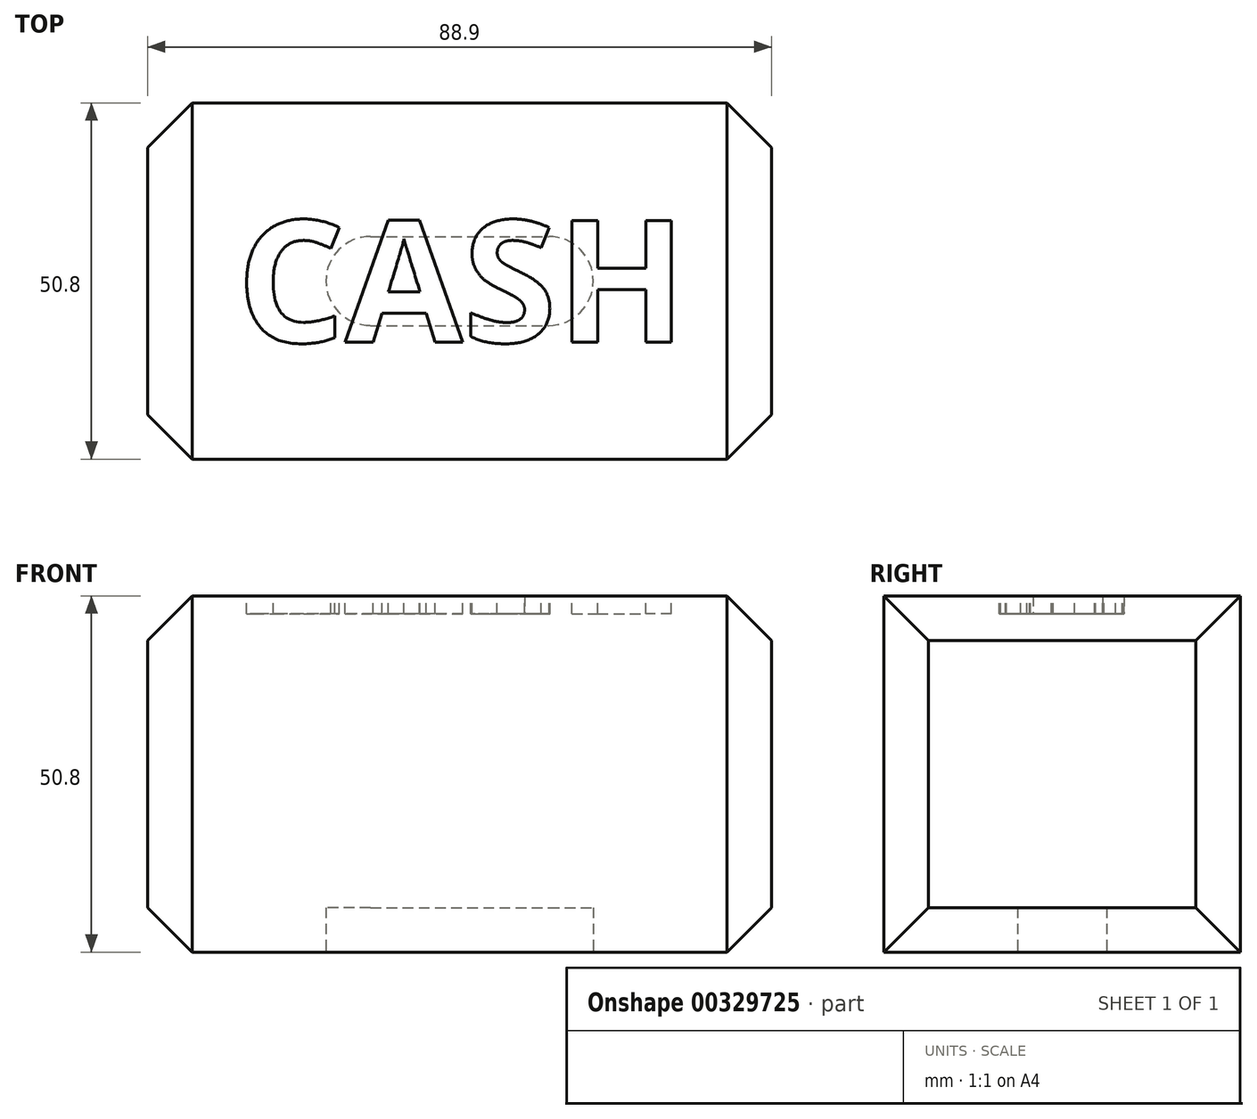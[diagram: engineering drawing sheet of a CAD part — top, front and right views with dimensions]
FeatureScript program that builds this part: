
annotation { "Feature Type Name" : "Feature", "Feature Type Description" : "" }
export const myFeature = defineFeature(function(context is Context, id is Id, definition is map)
    precondition{}
    {
        {
            var Q0;
            Q0=qCreatedBy(makeId("Front.planeOp"),FACE);
            var sketch = newSketch(context, id + "F0", { "sketchPlane" : qUnion([Q0])});
            skLineSegment(sketch, "E0.bottom", {"start": v(-44.45, 50.8) * mm, "end": v(44.45, 50.8) * mm});
            skLineSegment(sketch, "E0.top", {"start": v(-44.45, 0) * mm, "end": v(44.45, 0) * mm});
            skLineSegment(sketch, "E0.left", {"start": v(-44.45, 50.8) * mm, "end": v(-44.45, 0) * mm});
            skLineSegment(sketch, "E0.right", {"start": v(44.45, 50.8) * mm, "end": v(44.45, 0) * mm});
            skSolve(sketch);
        }
        {
            var Q0;
            Q0=makeQuery(id+"F0.imprint","IMPRINT",FACE,{"disambiguationData":[TD([[makeQuery(id+"F0.imprint","IMPRINT",EDGE,{"derivedFrom":sQuery(id+"F0.wireOp",EDGE,"E0.bottom")}),-1.0]])]});
            extrude(context, id + "F1", {"entities" : qUnion([Q0]), "endBound" : BoundingType.SYMMETRIC, "depth" : 50.8 * mm});
        }
        {
            var Q0;
            Q0=makeQuery(id+"F1.opExtrude","CAP_EDGE",EDGE,{"disambiguationData":[OSD([sQuery(id+"F0.wireOp",EDGE,"E0.left")])],"isStart":false});
            var Q1;
            Q1=makeQuery(id+"F1.opExtrude","SWEPT_EDGE",EDGE,{"disambiguationData":[OSD([sQuery(id+"F0.wireOp",EDGE,"E0.bottom"),sQuery(id+"F0.wireOp",EDGE,"E0.left")])]});
            var Q2;
            Q2=makeQuery(id+"F1.opExtrude","CAP_EDGE",EDGE,{"disambiguationData":[OSD([sQuery(id+"F0.wireOp",EDGE,"E0.left")])],"isStart":true});
            var Q3;
            Q3=makeQuery(id+"F1.opExtrude","SWEPT_FACE",FACE,{"disambiguationData":[OSD([sQuery(id+"F0.wireOp",EDGE,"E0.left")])]});
            var Q4;
            Q4=makeQuery(id+"F1.opExtrude","SWEPT_FACE",FACE,{"disambiguationData":[OSD([sQuery(id+"F0.wireOp",EDGE,"E0.right")])]});
            chamfer(context, id + "F2", {"entities" : qUnion([Q0, Q1, Q2, Q3, Q4]), "width" : 6.35 * mm, "tangentPropagation" : true});
        }
        {
            var Q0;
            Q0=makeQuery(id+"F1.opExtrude","SWEPT_FACE",FACE,{"disambiguationData":[OSD([sQuery(id+"F0.wireOp",EDGE,"E0.top")])]});
            var sketch = newSketch(context, id + "F3", { "sketchPlane" : qUnion([Q0])});
            skLineSegment(sketch, "E1", {"start": v(-12.7, 0) * mm, "end": v(12.7, 0) * mm, "construction": true});
            skLineSegment(sketch, "E2", {"start": v(-12.7, 6.35) * mm, "end": v(12.7, 6.35) * mm});
            skLineSegment(sketch, "E3", {"start": v(0, 0) * mm, "end": v(0, 6.35) * mm, "construction": true});
            skLineSegment(sketch, "E4", {"start": v(-12.7, -6.35) * mm, "end": v(12.7, -6.35) * mm});
            skLineSegment(sketch, "E5", {"start": v(0, 0) * mm, "end": v(0, -6.35) * mm, "construction": true});
            skArc(sketch, "E6", {"start": v(-12.7, 6.35) * mm, "mid": v(-19.05, 0) * mm, "end": v(-12.7, -6.35) * mm});
            skArc(sketch, "E7", {"start": v(12.7, -6.35) * mm, "mid": v(19.05, 0) * mm, "end": v(12.7, 6.35) * mm});
            skSolve(sketch);
        }
        {
            var Q0;
            Q0=makeQuery(id+"F3.imprint","IMPRINT",FACE,{"disambiguationData":[TD([[makeQuery(id+"F3.imprint","IMPRINT",EDGE,{"derivedFrom":sQuery(id+"F3.wireOp",EDGE,"E2")}),-1.0]])]});
            extrude(context, id + "F4", {"entities" : qUnion([Q0]), "operationType" : NewBodyOperationType.REMOVE, "oppositeDirection" : true, "depth" : 6.35 * mm});
        }
        {
            var Q0;
            Q0=makeQuery(id+"F1.opExtrude","SWEPT_FACE",FACE,{"disambiguationData":[OSD([sQuery(id+"F0.wireOp",EDGE,"E0.bottom")])]});
            var sketch = newSketch(context, id + "F5", { "sketchPlane" : qUnion([Q0])});
            skText(sketch, "E8", { "text": "CASH", "fontName": "OpenSans-Bold.ttf"});
            const initialGuessF5  = {"E8": [-0.03175, -0.00873, 1, 0, 0.01747]};
            skSetInitialGuess(sketch, initialGuessF5);
            skSolve(sketch);
        }
        {
            var Q0;
            Q0 = qSketchRegion(id + "F5", true);
            extrude(context, id + "F6", {"entities" : qUnion([Q0]), "operationType" : NewBodyOperationType.REMOVE, "oppositeDirection" : true, "depth" : 2.54 * mm});
        }
    });
